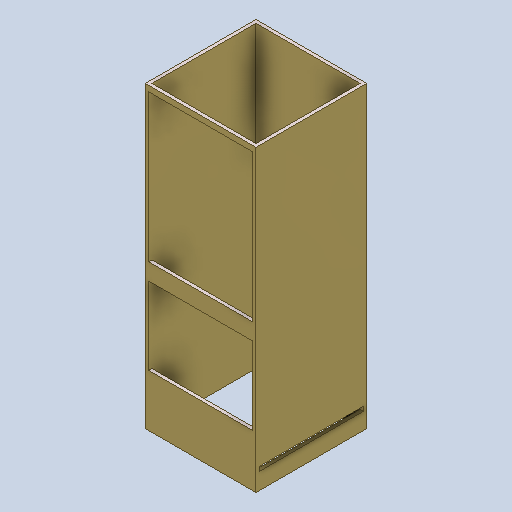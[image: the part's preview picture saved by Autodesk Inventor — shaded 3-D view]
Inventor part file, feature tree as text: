
AUTODESK INVENTOR PART (.ipt)
format: ipt  version: 2024.3 (Build 283343000, 343)  size: 270,848 bytes
history: native  units: mm
features: extrude x3, sketch x3
ambient origin geometry x8: Origin, YZ Plane, XZ Plane, XY Plane, X Axis, Y Axis, Z Axis, Center Point
bodies: Solid1 (feature_tree)
feature tree (6):
  extrude  "Extrusion1"  Depth=100.0mm
  extrude  "Extrusion2"  Depth=3.0mm
  extrude  "Extrusion10"  Depth=94.0mm
  sketch  "Sketch1"  dims[d0=100.0mm d1=100.0mm]
  sketch  "Sketch2"  dims[d2=3.0mm d3=3.0mm]
  sketch  "Sketch10"  dims[d4=270.0mm d5=0.0mm d6=94.0mm d7=3.0mm d8=5.0mm d9=133.0mm d10=70.0mm d11=15.0mm d12=3.0mm d13=10.0mm d14=0.0mm d46=4.0mm d47=10.0mm d48=0.0mm d49=15.0mm]
